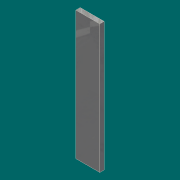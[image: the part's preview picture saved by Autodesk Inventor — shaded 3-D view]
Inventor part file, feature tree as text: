
AUTODESK INVENTOR PART (.ipt)
format: ipt  version: 2017 (Build 210142000, 142)  size: 71,168 bytes
history: native  units: in
note: dims shown in document units (in); Inventor stores cm internally (conversion verified against a paired STEP export)
features: extrude x1, sketch x1
ambient origin geometry x8: Origin, YZ Plane, XZ Plane, XY Plane, X Axis, Y Axis, Z Axis, Center Point
bodies: Solid1 (feature_tree)
feature tree (2):
  extrude  "Extrusion1"  Depth=3.5in
  sketch  "Sketch1"  dims[d0=0.65in d1=3.5in d2=0.12in d3=0.0in]
